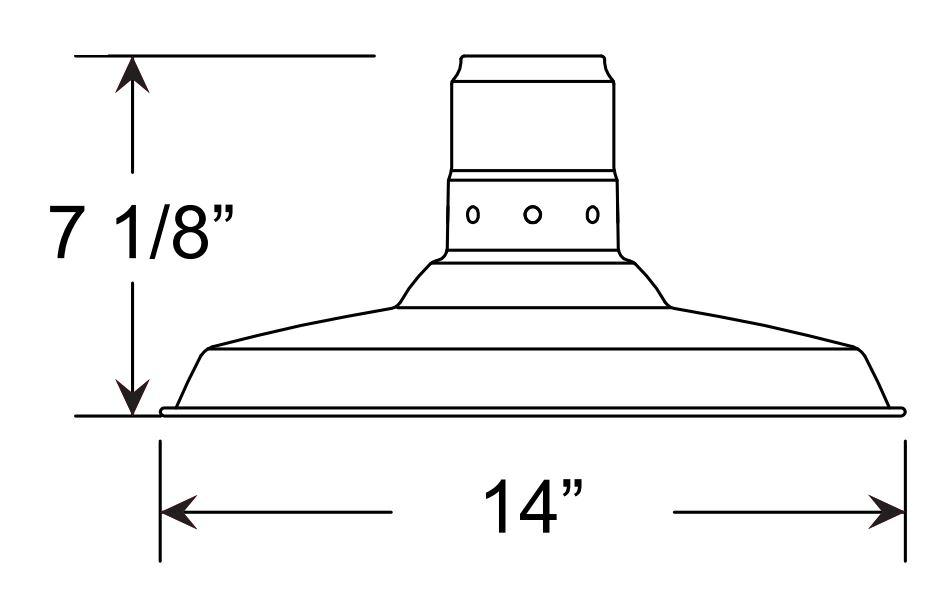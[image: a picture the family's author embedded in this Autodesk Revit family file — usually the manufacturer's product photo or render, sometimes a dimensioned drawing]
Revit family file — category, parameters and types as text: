
# Revit family: Deep Bowl led
name_source: partatom
category: Lighting Fixtures
units: mm (PartAtom-declared; Revit-internal decimal feet)

## family parameters
Always vertical = Yes
Cut with Voids When Loaded = No
Light Source = Yes
OmniClass Number = 23.80.70.00
OmniClass Title = Lighting
Part Type = Normal
Room Calculation Point = No
Round Connector Dimension = Use Diameter
Shared = No
Work Plane-Based = No

## types (9) — shared parameters
BULB = Yes
Body Colour = Spun aluminium
Body Material = body
Bulb = Bulb
CRI = >90
Color Filter = 16777215
Construction Material = Heavy Duty spun aluminum.
Default Elevation = 0' - 0"
Description = 120-277 Voltage
Dimming = 1%
Dimming Lamp Color Temperature Shift = <None>
Efficiency = 65-125 lumens per watt
Lamp = LED
Life = L70 50,000 hours
Load Classification = Lighting
Manufacturer = ANP Lighting
Power Factor = 1
Tilt Angle = 90.00°
URL = https://www.anplighting.com
Voltage = 277 V
Warranty = 5 year limited warranty
b = 0' - 3"

## per-type parameters (varying)
| type | Apparent Load | D608 | D610 | D612 | D616 | D618 | Fixture Diameter | Fixture Height | OSD622 | OSD626 | OSD630 | OSD638 | Photometric Web File | Wattage Comments | Weight | a |
| D608 | 9 VA | Yes | No | No | No | No | 0' - 8" | 0' - 7 1/2" | No | No | No | No | D608M009LDNW40K (1).IES | 9W | 1.0lbs | 0' - 8" |
| D610 | 10 VA | No | Yes | No | No | No | 0' - 10" | 1' - 0" | No | No | No | No | D610M010LDDW40K.IES | 10W | 1.0lbs | 0' - 9" |
| D612 | 16 VA | No | No | Yes | No | No | 1' - 0" | 0' - 11" | No | No | No | No | D612-100GLCL-32WPL.IES | 16W | 1.0lbs | 0' - 10" |
| D616 | 16 VA | No | No | No | Yes | No | 1' - 4" | 1' - 1 1/4" | No | No | No | No | D616M016LDNW40K (1).IES | 16W | 1.5lbs | 0' - 10" |
| D618 | 10 VA | No | No | No | No | Yes | 1' - 6" | 1' - 4" | No | No | No | No | D618M010LDNW30K.IES | 10W | 2.5 lbs | 1' - 0" |
| OSD622 | 37 VA | No | No | No | No | No | 1' - 10" | 1' - 8" | Yes | No | No | No | D618M016LDNW30K.IES | 37W | 12.5lbs | 1' - 7" |
| OSD630 | 37 VA | No | No | No | No | No | 2' - 6" | 2' - 3" | No | No | Yes | No | D618M016LDNW30K.IES | 37W | 18.0 lbs | 1' - 7" |
| OSD638 | 37 VA | No | No | No | No | No | 3' - 2" | 2' - 7" | No | No | No | Yes | D618M016LDNW30K.IES | 37W | 25.0 lbs | 1' - 6" |
| OSD626 | 37 VA | No | No | No | No | No | 2' - 2" | 1' - 11" | No | Yes | No | No | D618M016LDNW30K.IES | 37W | 15 lbS | 1' - 7" |

note: column(s) folded — value = type name in every type: Model

## geometry (parser evidence)
native form markers: Sweep x70
no freeform markers — native parametric forms only
